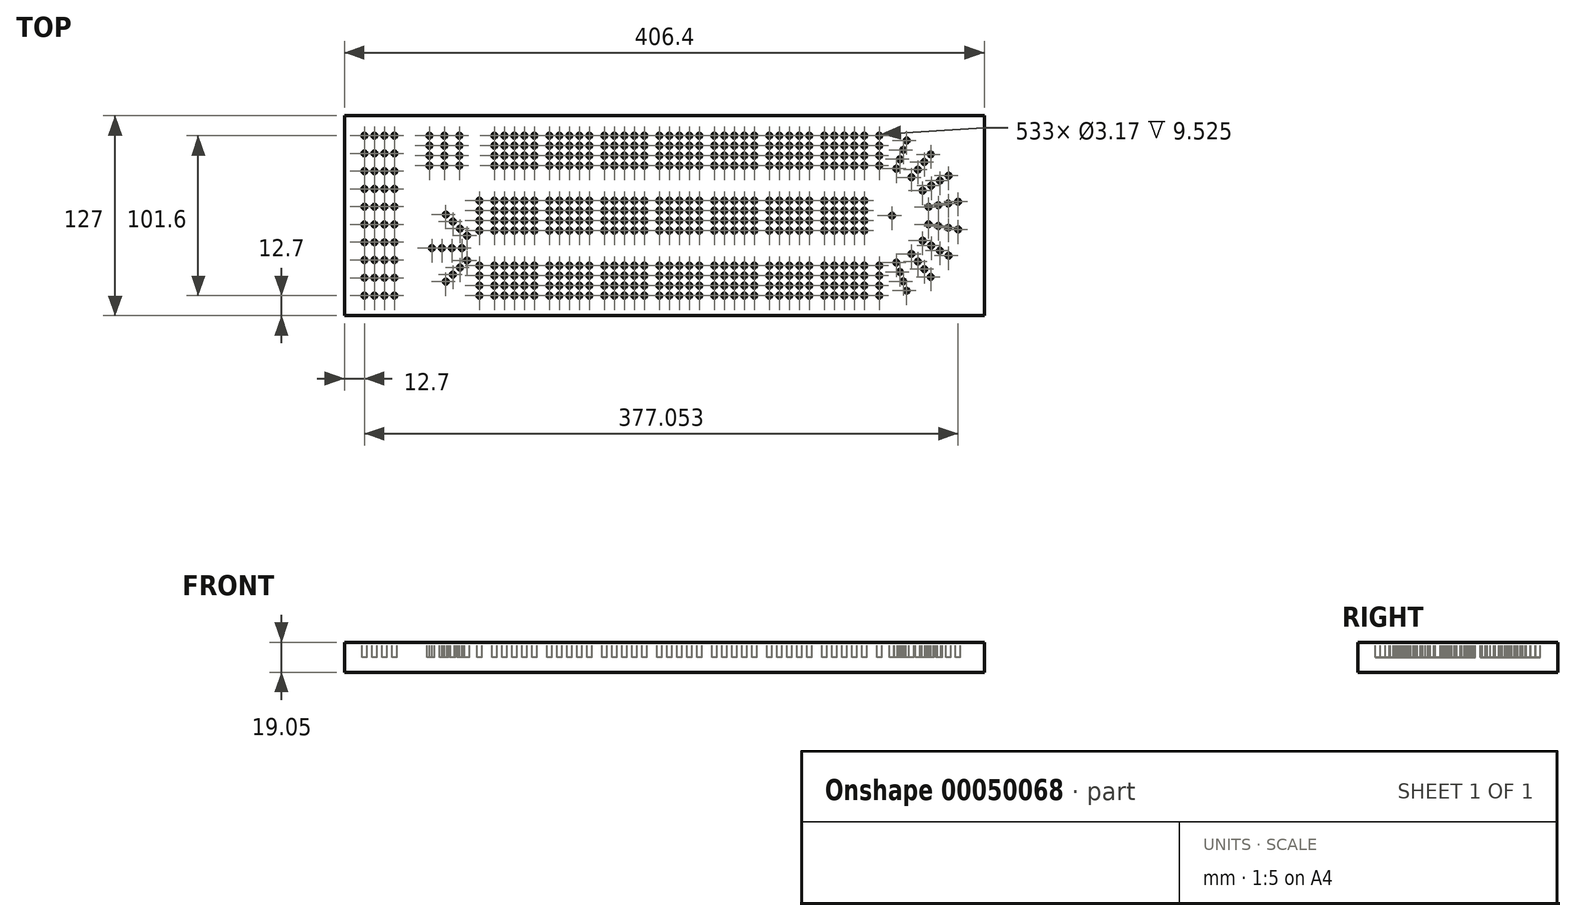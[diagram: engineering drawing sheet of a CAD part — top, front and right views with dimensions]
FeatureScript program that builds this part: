
annotation { "Feature Type Name" : "Feature", "Feature Type Description" : "" }
export const myFeature = defineFeature(function(context is Context, id is Id, definition is map)
    precondition{}
    {
        {
            var Q0;
            Q0=qCreatedBy(makeId("Top.planeOp"),FACE);
            var sketch = newSketch(context, id + "F0", { "sketchPlane" : qUnion([Q0])});
            skLineSegment(sketch, "E0.bottom", {"start": v(0, 0) * mm, "end": v(381, 0) * mm});
            skLineSegment(sketch, "E0.top", {"start": v(0, 127) * mm, "end": v(381, 127) * mm});
            skLineSegment(sketch, "E0.right", {"start": v(381, 0) * mm, "end": v(381, 127) * mm});
            skLineSegment(sketch, "E1", {"start": v(0, 127) * mm, "end": v(-25.4, 127) * mm});
            skLineSegment(sketch, "E2", {"start": v(-25.4, 127) * mm, "end": v(-25.4, 0) * mm});
            skLineSegment(sketch, "E3", {"start": v(-25.4, 0) * mm, "end": v(0, 0) * mm});
            skSolve(sketch);
        }
        {
            var Q0;
            Q0 = qSketchRegion(id + "F0", true);
            extrude(context, id + "F1", {"entities" : qUnion([Q0]), "depth" : 19.05 * mm});
        }
        {
            var Q0;
            Q0=makeQuery(id+"F1.opExtrude","CAP_FACE",FACE,{"disambiguationData":[OSD([sQuery(id+"F0.wireOp",EDGE,"E0.bottom"),sQuery(id+"F0.wireOp",EDGE,"E0.top"),sQuery(id+"F0.wireOp",EDGE,"E0.left"),sQuery(id+"F0.wireOp",EDGE,"E0.right")])],"isStart":false});
            var sketch = newSketch(context, id + "F2", { "sketchPlane" : qUnion([Q0])});
            skCircle(sketch, "E4", {"center": v(69.85, 114.3) * mm, "radius": 1.59 * mm});
            skCircle(sketch, "E5.0.1.0", {"center": v(69.85, 107.95) * mm, "radius": 1.59 * mm});
            skCircle(sketch, "E5.0.2.0", {"center": v(69.85, 101.6) * mm, "radius": 1.59 * mm});
            skCircle(sketch, "E5.0.3.0", {"center": v(69.85, 95.25) * mm, "radius": 1.59 * mm});
            skCircle(sketch, "E5.1.0.0", {"center": v(76.2, 114.3) * mm, "radius": 1.59 * mm});
            skCircle(sketch, "E5.1.1.0", {"center": v(76.2, 107.95) * mm, "radius": 1.59 * mm});
            skCircle(sketch, "E5.1.2.0", {"center": v(76.2, 101.6) * mm, "radius": 1.59 * mm});
            skCircle(sketch, "E5.1.3.0", {"center": v(76.2, 95.25) * mm, "radius": 1.59 * mm});
            skCircle(sketch, "E5.2.0.0", {"center": v(82.55, 114.3) * mm, "radius": 1.59 * mm});
            skCircle(sketch, "E5.2.1.0", {"center": v(82.55, 107.95) * mm, "radius": 1.59 * mm});
            skCircle(sketch, "E5.2.2.0", {"center": v(82.55, 101.6) * mm, "radius": 1.59 * mm});
            skCircle(sketch, "E5.2.3.0", {"center": v(82.55, 95.25) * mm, "radius": 1.59 * mm});
            skCircle(sketch, "E5.3.0.0", {"center": v(88.9, 114.3) * mm, "radius": 1.59 * mm});
            skCircle(sketch, "E5.3.1.0", {"center": v(88.9, 107.95) * mm, "radius": 1.59 * mm});
            skCircle(sketch, "E5.3.2.0", {"center": v(88.9, 101.6) * mm, "radius": 1.59 * mm});
            skCircle(sketch, "E5.3.3.0", {"center": v(88.9, 95.25) * mm, "radius": 1.59 * mm});
            skCircle(sketch, "E5.4.0.0", {"center": v(95.25, 114.3) * mm, "radius": 1.59 * mm});
            skCircle(sketch, "E5.4.1.0", {"center": v(95.25, 107.95) * mm, "radius": 1.59 * mm});
            skCircle(sketch, "E5.4.2.0", {"center": v(95.25, 101.6) * mm, "radius": 1.59 * mm});
            skCircle(sketch, "E5.4.3.0", {"center": v(95.25, 95.25) * mm, "radius": 1.59 * mm});
            skLineSegment(sketch, "E5.direction1", {"start": v(69.85, 114.3) * mm, "end": v(76.2, 114.3) * mm, "construction": true});
            skLineSegment(sketch, "E5.direction2", {"start": v(69.85, 114.3) * mm, "end": v(69.85, 107.95) * mm, "construction": true});
            skCircle(sketch, "E6.1.0.0", {"center": v(123.82, 95.25) * mm, "radius": 1.59 * mm});
            skCircle(sketch, "E6.1.0.1", {"center": v(117.47, 95.25) * mm, "radius": 1.59 * mm});
            skCircle(sketch, "E6.1.0.2", {"center": v(117.47, 114.3) * mm, "radius": 1.59 * mm});
            skCircle(sketch, "E6.1.0.3", {"center": v(130.17, 95.25) * mm, "radius": 1.59 * mm});
            skCircle(sketch, "E6.1.0.4", {"center": v(117.47, 107.95) * mm, "radius": 1.59 * mm});
            skCircle(sketch, "E6.1.0.5", {"center": v(130.17, 114.3) * mm, "radius": 1.59 * mm});
            skCircle(sketch, "E6.1.0.6", {"center": v(123.82, 114.3) * mm, "radius": 1.59 * mm});
            skCircle(sketch, "E6.1.0.7", {"center": v(123.82, 107.95) * mm, "radius": 1.59 * mm});
            skCircle(sketch, "E6.1.0.8", {"center": v(111.12, 95.25) * mm, "radius": 1.59 * mm});
            skCircle(sketch, "E6.1.0.9", {"center": v(123.82, 101.6) * mm, "radius": 1.59 * mm});
            skCircle(sketch, "E6.1.0.10", {"center": v(130.17, 107.95) * mm, "radius": 1.59 * mm});
            skCircle(sketch, "E6.1.0.11", {"center": v(111.12, 107.95) * mm, "radius": 1.59 * mm});
            skCircle(sketch, "E6.1.0.12", {"center": v(117.47, 101.6) * mm, "radius": 1.59 * mm});
            skCircle(sketch, "E6.1.0.13", {"center": v(104.78, 101.6) * mm, "radius": 1.59 * mm});
            skCircle(sketch, "E6.1.0.14", {"center": v(130.17, 101.6) * mm, "radius": 1.59 * mm});
            skCircle(sketch, "E6.1.0.15", {"center": v(111.12, 101.6) * mm, "radius": 1.59 * mm});
            skLineSegment(sketch, "E6.1.0.16", {"start": v(104.78, 114.3) * mm, "end": v(111.12, 114.3) * mm, "construction": true});
            skCircle(sketch, "E6.1.0.17", {"center": v(111.12, 114.3) * mm, "radius": 1.59 * mm});
            skLineSegment(sketch, "E6.1.0.18", {"start": v(104.78, 114.3) * mm, "end": v(104.78, 107.95) * mm, "construction": true});
            skCircle(sketch, "E6.1.0.19", {"center": v(104.78, 107.95) * mm, "radius": 1.59 * mm});
            skCircle(sketch, "E6.1.0.20", {"center": v(104.78, 114.3) * mm, "radius": 1.59 * mm});
            skCircle(sketch, "E6.1.0.21", {"center": v(104.78, 95.25) * mm, "radius": 1.59 * mm});
            skCircle(sketch, "E6.2.0.0", {"center": v(158.75, 95.25) * mm, "radius": 1.59 * mm});
            skCircle(sketch, "E6.2.0.1", {"center": v(152.4, 95.25) * mm, "radius": 1.59 * mm});
            skCircle(sketch, "E6.2.0.2", {"center": v(152.4, 114.3) * mm, "radius": 1.59 * mm});
            skCircle(sketch, "E6.2.0.3", {"center": v(165.1, 95.25) * mm, "radius": 1.59 * mm});
            skCircle(sketch, "E6.2.0.4", {"center": v(152.4, 107.95) * mm, "radius": 1.59 * mm});
            skCircle(sketch, "E6.2.0.5", {"center": v(165.1, 114.3) * mm, "radius": 1.59 * mm});
            skCircle(sketch, "E6.2.0.6", {"center": v(158.75, 114.3) * mm, "radius": 1.59 * mm});
            skCircle(sketch, "E6.2.0.7", {"center": v(158.75, 107.95) * mm, "radius": 1.59 * mm});
            skCircle(sketch, "E6.2.0.8", {"center": v(146.05, 95.25) * mm, "radius": 1.59 * mm});
            skCircle(sketch, "E6.2.0.9", {"center": v(158.75, 101.6) * mm, "radius": 1.59 * mm});
            skCircle(sketch, "E6.2.0.10", {"center": v(165.1, 107.95) * mm, "radius": 1.59 * mm});
            skCircle(sketch, "E6.2.0.11", {"center": v(146.05, 107.95) * mm, "radius": 1.59 * mm});
            skCircle(sketch, "E6.2.0.12", {"center": v(152.4, 101.6) * mm, "radius": 1.59 * mm});
            skCircle(sketch, "E6.2.0.13", {"center": v(139.7, 101.6) * mm, "radius": 1.59 * mm});
            skCircle(sketch, "E6.2.0.14", {"center": v(165.1, 101.6) * mm, "radius": 1.59 * mm});
            skCircle(sketch, "E6.2.0.15", {"center": v(146.05, 101.6) * mm, "radius": 1.59 * mm});
            skLineSegment(sketch, "E6.2.0.16", {"start": v(139.7, 114.3) * mm, "end": v(146.05, 114.3) * mm, "construction": true});
            skCircle(sketch, "E6.2.0.17", {"center": v(146.05, 114.3) * mm, "radius": 1.59 * mm});
            skLineSegment(sketch, "E6.2.0.18", {"start": v(139.7, 114.3) * mm, "end": v(139.7, 107.95) * mm, "construction": true});
            skCircle(sketch, "E6.2.0.19", {"center": v(139.7, 107.95) * mm, "radius": 1.59 * mm});
            skCircle(sketch, "E6.2.0.20", {"center": v(139.7, 114.3) * mm, "radius": 1.59 * mm});
            skCircle(sketch, "E6.2.0.21", {"center": v(139.7, 95.25) * mm, "radius": 1.59 * mm});
            skCircle(sketch, "E6.3.0.0", {"center": v(193.68, 95.25) * mm, "radius": 1.59 * mm});
            skCircle(sketch, "E6.3.0.1", {"center": v(187.33, 95.25) * mm, "radius": 1.59 * mm});
            skCircle(sketch, "E6.3.0.2", {"center": v(187.33, 114.3) * mm, "radius": 1.59 * mm});
            skCircle(sketch, "E6.3.0.3", {"center": v(200.03, 95.25) * mm, "radius": 1.59 * mm});
            skCircle(sketch, "E6.3.0.4", {"center": v(187.33, 107.95) * mm, "radius": 1.59 * mm});
            skCircle(sketch, "E6.3.0.5", {"center": v(200.03, 114.3) * mm, "radius": 1.59 * mm});
            skCircle(sketch, "E6.3.0.6", {"center": v(193.68, 114.3) * mm, "radius": 1.59 * mm});
            skCircle(sketch, "E6.3.0.7", {"center": v(193.68, 107.95) * mm, "radius": 1.59 * mm});
            skCircle(sketch, "E6.3.0.8", {"center": v(180.98, 95.25) * mm, "radius": 1.59 * mm});
            skCircle(sketch, "E6.3.0.9", {"center": v(193.68, 101.6) * mm, "radius": 1.59 * mm});
            skCircle(sketch, "E6.3.0.10", {"center": v(200.03, 107.95) * mm, "radius": 1.59 * mm});
            skCircle(sketch, "E6.3.0.11", {"center": v(180.98, 107.95) * mm, "radius": 1.59 * mm});
            skCircle(sketch, "E6.3.0.12", {"center": v(187.33, 101.6) * mm, "radius": 1.59 * mm});
            skCircle(sketch, "E6.3.0.13", {"center": v(174.63, 101.6) * mm, "radius": 1.59 * mm});
            skCircle(sketch, "E6.3.0.14", {"center": v(200.03, 101.6) * mm, "radius": 1.59 * mm});
            skCircle(sketch, "E6.3.0.15", {"center": v(180.98, 101.6) * mm, "radius": 1.59 * mm});
            skLineSegment(sketch, "E6.3.0.16", {"start": v(174.63, 114.3) * mm, "end": v(180.97, 114.3) * mm, "construction": true});
            skCircle(sketch, "E6.3.0.17", {"center": v(180.98, 114.3) * mm, "radius": 1.59 * mm});
            skLineSegment(sketch, "E6.3.0.18", {"start": v(174.63, 114.3) * mm, "end": v(174.63, 107.95) * mm, "construction": true});
            skCircle(sketch, "E6.3.0.19", {"center": v(174.63, 107.95) * mm, "radius": 1.59 * mm});
            skCircle(sketch, "E6.3.0.20", {"center": v(174.63, 114.3) * mm, "radius": 1.59 * mm});
            skCircle(sketch, "E6.3.0.21", {"center": v(174.63, 95.25) * mm, "radius": 1.59 * mm});
            skCircle(sketch, "E6.4.0.0", {"center": v(228.6, 95.25) * mm, "radius": 1.59 * mm});
            skCircle(sketch, "E6.4.0.1", {"center": v(222.25, 95.25) * mm, "radius": 1.59 * mm});
            skCircle(sketch, "E6.4.0.2", {"center": v(222.25, 114.3) * mm, "radius": 1.59 * mm});
            skCircle(sketch, "E6.4.0.3", {"center": v(234.95, 95.25) * mm, "radius": 1.59 * mm});
            skCircle(sketch, "E6.4.0.4", {"center": v(222.25, 107.95) * mm, "radius": 1.59 * mm});
            skCircle(sketch, "E6.4.0.5", {"center": v(234.95, 114.3) * mm, "radius": 1.59 * mm});
            skCircle(sketch, "E6.4.0.6", {"center": v(228.6, 114.3) * mm, "radius": 1.59 * mm});
            skCircle(sketch, "E6.4.0.7", {"center": v(228.6, 107.95) * mm, "radius": 1.59 * mm});
            skCircle(sketch, "E6.4.0.8", {"center": v(215.9, 95.25) * mm, "radius": 1.59 * mm});
            skCircle(sketch, "E6.4.0.9", {"center": v(228.6, 101.6) * mm, "radius": 1.59 * mm});
            skCircle(sketch, "E6.4.0.10", {"center": v(234.95, 107.95) * mm, "radius": 1.59 * mm});
            skCircle(sketch, "E6.4.0.11", {"center": v(215.9, 107.95) * mm, "radius": 1.59 * mm});
            skCircle(sketch, "E6.4.0.12", {"center": v(222.25, 101.6) * mm, "radius": 1.59 * mm});
            skCircle(sketch, "E6.4.0.13", {"center": v(209.55, 101.6) * mm, "radius": 1.59 * mm});
            skCircle(sketch, "E6.4.0.14", {"center": v(234.95, 101.6) * mm, "radius": 1.59 * mm});
            skCircle(sketch, "E6.4.0.15", {"center": v(215.9, 101.6) * mm, "radius": 1.59 * mm});
            skLineSegment(sketch, "E6.4.0.16", {"start": v(209.55, 114.3) * mm, "end": v(215.9, 114.3) * mm, "construction": true});
            skCircle(sketch, "E6.4.0.17", {"center": v(215.9, 114.3) * mm, "radius": 1.59 * mm});
            skLineSegment(sketch, "E6.4.0.18", {"start": v(209.55, 114.3) * mm, "end": v(209.55, 107.95) * mm, "construction": true});
            skCircle(sketch, "E6.4.0.19", {"center": v(209.55, 107.95) * mm, "radius": 1.59 * mm});
            skCircle(sketch, "E6.4.0.20", {"center": v(209.55, 114.3) * mm, "radius": 1.59 * mm});
            skCircle(sketch, "E6.4.0.21", {"center": v(209.55, 95.25) * mm, "radius": 1.59 * mm});
            skCircle(sketch, "E6.5.0.0", {"center": v(263.53, 95.25) * mm, "radius": 1.59 * mm});
            skCircle(sketch, "E6.5.0.1", {"center": v(257.18, 95.25) * mm, "radius": 1.59 * mm});
            skCircle(sketch, "E6.5.0.2", {"center": v(257.18, 114.3) * mm, "radius": 1.59 * mm});
            skCircle(sketch, "E6.5.0.3", {"center": v(269.88, 95.25) * mm, "radius": 1.59 * mm});
            skCircle(sketch, "E6.5.0.4", {"center": v(257.18, 107.95) * mm, "radius": 1.59 * mm});
            skCircle(sketch, "E6.5.0.5", {"center": v(269.88, 114.3) * mm, "radius": 1.59 * mm});
            skCircle(sketch, "E6.5.0.6", {"center": v(263.53, 114.3) * mm, "radius": 1.59 * mm});
            skCircle(sketch, "E6.5.0.7", {"center": v(263.53, 107.95) * mm, "radius": 1.59 * mm});
            skCircle(sketch, "E6.5.0.8", {"center": v(250.83, 95.25) * mm, "radius": 1.59 * mm});
            skCircle(sketch, "E6.5.0.9", {"center": v(263.53, 101.6) * mm, "radius": 1.59 * mm});
            skCircle(sketch, "E6.5.0.10", {"center": v(269.88, 107.95) * mm, "radius": 1.59 * mm});
            skCircle(sketch, "E6.5.0.11", {"center": v(250.83, 107.95) * mm, "radius": 1.59 * mm});
            skCircle(sketch, "E6.5.0.12", {"center": v(257.18, 101.6) * mm, "radius": 1.59 * mm});
            skCircle(sketch, "E6.5.0.13", {"center": v(244.48, 101.6) * mm, "radius": 1.59 * mm});
            skCircle(sketch, "E6.5.0.14", {"center": v(269.88, 101.6) * mm, "radius": 1.59 * mm});
            skCircle(sketch, "E6.5.0.15", {"center": v(250.83, 101.6) * mm, "radius": 1.59 * mm});
            skLineSegment(sketch, "E6.5.0.16", {"start": v(244.48, 114.3) * mm, "end": v(250.83, 114.3) * mm, "construction": true});
            skCircle(sketch, "E6.5.0.17", {"center": v(250.83, 114.3) * mm, "radius": 1.59 * mm});
            skLineSegment(sketch, "E6.5.0.18", {"start": v(244.48, 114.3) * mm, "end": v(244.48, 107.95) * mm, "construction": true});
            skCircle(sketch, "E6.5.0.19", {"center": v(244.48, 107.95) * mm, "radius": 1.59 * mm});
            skCircle(sketch, "E6.5.0.20", {"center": v(244.48, 114.3) * mm, "radius": 1.59 * mm});
            skCircle(sketch, "E6.5.0.21", {"center": v(244.48, 95.25) * mm, "radius": 1.59 * mm});
            skCircle(sketch, "E6.6.0.0", {"center": v(298.45, 95.25) * mm, "radius": 1.59 * mm});
            skCircle(sketch, "E6.6.0.1", {"center": v(292.1, 95.25) * mm, "radius": 1.59 * mm});
            skCircle(sketch, "E6.6.0.2", {"center": v(292.1, 114.3) * mm, "radius": 1.59 * mm});
            skCircle(sketch, "E6.6.0.3", {"center": v(304.8, 95.25) * mm, "radius": 1.59 * mm});
            skCircle(sketch, "E6.6.0.4", {"center": v(292.1, 107.95) * mm, "radius": 1.59 * mm});
            skCircle(sketch, "E6.6.0.5", {"center": v(304.8, 114.3) * mm, "radius": 1.59 * mm});
            skCircle(sketch, "E6.6.0.6", {"center": v(298.45, 114.3) * mm, "radius": 1.59 * mm});
            skCircle(sketch, "E6.6.0.7", {"center": v(298.45, 107.95) * mm, "radius": 1.59 * mm});
            skCircle(sketch, "E6.6.0.8", {"center": v(285.75, 95.25) * mm, "radius": 1.59 * mm});
            skCircle(sketch, "E6.6.0.9", {"center": v(298.45, 101.6) * mm, "radius": 1.59 * mm});
            skCircle(sketch, "E6.6.0.10", {"center": v(304.8, 107.95) * mm, "radius": 1.59 * mm});
            skCircle(sketch, "E6.6.0.11", {"center": v(285.75, 107.95) * mm, "radius": 1.59 * mm});
            skCircle(sketch, "E6.6.0.12", {"center": v(292.1, 101.6) * mm, "radius": 1.59 * mm});
            skCircle(sketch, "E6.6.0.13", {"center": v(279.4, 101.6) * mm, "radius": 1.59 * mm});
            skCircle(sketch, "E6.6.0.14", {"center": v(304.8, 101.6) * mm, "radius": 1.59 * mm});
            skCircle(sketch, "E6.6.0.15", {"center": v(285.75, 101.6) * mm, "radius": 1.59 * mm});
            skLineSegment(sketch, "E6.6.0.16", {"start": v(279.4, 114.3) * mm, "end": v(285.75, 114.3) * mm, "construction": true});
            skCircle(sketch, "E6.6.0.17", {"center": v(285.75, 114.3) * mm, "radius": 1.59 * mm});
            skLineSegment(sketch, "E6.6.0.18", {"start": v(279.4, 114.3) * mm, "end": v(279.4, 107.95) * mm, "construction": true});
            skCircle(sketch, "E6.6.0.19", {"center": v(279.4, 107.95) * mm, "radius": 1.59 * mm});
            skCircle(sketch, "E6.6.0.20", {"center": v(279.4, 114.3) * mm, "radius": 1.59 * mm});
            skCircle(sketch, "E6.6.0.21", {"center": v(279.4, 95.25) * mm, "radius": 1.59 * mm});
            skLineSegment(sketch, "E6.direction1", {"start": v(88.9, 95.25) * mm, "end": v(123.82, 95.25) * mm, "construction": true});
            skLineSegment(sketch, "E7.MirrorCS", {"start": v(69.85, 12.7) * mm, "end": v(69.85, 19.05) * mm, "construction": true});
            skCircle(sketch, "E8.MirrorC", {"center": v(174.63, 12.7) * mm, "radius": 1.59 * mm});
            skLineSegment(sketch, "E9.MirrorCS", {"start": v(279.4, 12.7) * mm, "end": v(279.4, 19.05) * mm, "construction": true});
            skLineSegment(sketch, "E10.MirrorCS", {"start": v(104.78, 12.7) * mm, "end": v(104.78, 19.05) * mm, "construction": true});
            skLineSegment(sketch, "E11.MirrorCS", {"start": v(209.55, 12.7) * mm, "end": v(215.9, 12.7) * mm, "construction": true});
            skCircle(sketch, "E12.MirrorC", {"center": v(279.4, 12.7) * mm, "radius": 1.59 * mm});
            skCircle(sketch, "E13.MirrorC", {"center": v(104.78, 12.7) * mm, "radius": 1.59 * mm});
            skLineSegment(sketch, "E14.MirrorCS", {"start": v(209.55, 12.7) * mm, "end": v(209.55, 19.05) * mm, "construction": true});
            skLineSegment(sketch, "E15.MirrorCS", {"start": v(139.7, 12.7) * mm, "end": v(146.05, 12.7) * mm, "construction": true});
            skCircle(sketch, "E16.MirrorC", {"center": v(209.55, 12.7) * mm, "radius": 1.59 * mm});
            skLineSegment(sketch, "E17.MirrorCS", {"start": v(139.7, 12.7) * mm, "end": v(139.7, 19.05) * mm, "construction": true});
            skLineSegment(sketch, "E18.MirrorCS", {"start": v(244.48, 12.7) * mm, "end": v(250.83, 12.7) * mm, "construction": true});
            skCircle(sketch, "E19.MirrorC", {"center": v(139.7, 12.7) * mm, "radius": 1.59 * mm});
            skCircle(sketch, "E20.MirrorC", {"center": v(69.85, 12.7) * mm, "radius": 1.59 * mm});
            skLineSegment(sketch, "E21.MirrorCS", {"start": v(244.48, 12.7) * mm, "end": v(244.48, 19.05) * mm, "construction": true});
            skCircle(sketch, "E22.MirrorC", {"center": v(244.48, 12.7) * mm, "radius": 1.59 * mm});
            skLineSegment(sketch, "E23.MirrorCS", {"start": v(174.63, 12.7) * mm, "end": v(180.97, 12.7) * mm, "construction": true});
            skLineSegment(sketch, "E24.MirrorCS", {"start": v(174.63, 12.7) * mm, "end": v(174.63, 19.05) * mm, "construction": true});
            skLineSegment(sketch, "E25.MirrorCS", {"start": v(69.85, 12.7) * mm, "end": v(76.2, 12.7) * mm, "construction": true});
            skCircle(sketch, "E26.MirrorC", {"center": v(174.63, 19.05) * mm, "radius": 1.59 * mm});
            skCircle(sketch, "E27.MirrorC", {"center": v(285.75, 12.7) * mm, "radius": 1.59 * mm});
            skCircle(sketch, "E28.MirrorC", {"center": v(111.12, 12.7) * mm, "radius": 1.59 * mm});
            skCircle(sketch, "E29.MirrorC", {"center": v(279.4, 19.05) * mm, "radius": 1.59 * mm});
            skLineSegment(sketch, "E30.MirrorCS", {"start": v(104.78, 12.7) * mm, "end": v(111.12, 12.7) * mm, "construction": true});
            skCircle(sketch, "E31.MirrorC", {"center": v(123.82, 31.75) * mm, "radius": 1.59 * mm});
            skCircle(sketch, "E32.MirrorC", {"center": v(104.78, 19.05) * mm, "radius": 1.59 * mm});
            skCircle(sketch, "E33.MirrorC", {"center": v(215.9, 12.7) * mm, "radius": 1.59 * mm});
            skCircle(sketch, "E34.MirrorC", {"center": v(209.55, 19.05) * mm, "radius": 1.59 * mm});
            skCircle(sketch, "E35.MirrorC", {"center": v(146.05, 12.7) * mm, "radius": 1.59 * mm});
            skCircle(sketch, "E36.MirrorC", {"center": v(139.7, 19.05) * mm, "radius": 1.59 * mm});
            skCircle(sketch, "E37.MirrorC", {"center": v(88.9, 31.75) * mm, "radius": 1.59 * mm});
            skCircle(sketch, "E38.MirrorC", {"center": v(250.83, 12.7) * mm, "radius": 1.59 * mm});
            skCircle(sketch, "E39.MirrorC", {"center": v(69.85, 19.05) * mm, "radius": 1.59 * mm});
            skCircle(sketch, "E40.MirrorC", {"center": v(180.98, 12.7) * mm, "radius": 1.59 * mm});
            skLineSegment(sketch, "E41.MirrorCS", {"start": v(279.4, 12.7) * mm, "end": v(285.75, 12.7) * mm, "construction": true});
            skCircle(sketch, "E42.MirrorC", {"center": v(76.2, 12.7) * mm, "radius": 1.59 * mm});
            skCircle(sketch, "E43.MirrorC", {"center": v(244.48, 19.05) * mm, "radius": 1.59 * mm});
            skCircle(sketch, "E44.MirrorC", {"center": v(111.12, 25.4) * mm, "radius": 1.59 * mm});
            skCircle(sketch, "E45.MirrorC", {"center": v(76.2, 19.05) * mm, "radius": 1.59 * mm});
            skCircle(sketch, "E46.MirrorC", {"center": v(209.55, 25.4) * mm, "radius": 1.59 * mm});
            skCircle(sketch, "E47.MirrorC", {"center": v(200.03, 31.75) * mm, "radius": 1.59 * mm});
            skCircle(sketch, "E48.MirrorC", {"center": v(158.75, 25.4) * mm, "radius": 1.59 * mm});
            skCircle(sketch, "E49.MirrorC", {"center": v(292.1, 31.75) * mm, "radius": 1.59 * mm});
            skCircle(sketch, "E50.MirrorC", {"center": v(263.53, 19.05) * mm, "radius": 1.59 * mm});
            skCircle(sketch, "E51.MirrorC", {"center": v(146.05, 19.05) * mm, "radius": 1.59 * mm});
            skCircle(sketch, "E52.MirrorC", {"center": v(117.47, 31.75) * mm, "radius": 1.59 * mm});
            skCircle(sketch, "E53.MirrorC", {"center": v(76.2, 31.75) * mm, "radius": 1.59 * mm});
            skCircle(sketch, "E54.MirrorC", {"center": v(263.53, 25.4) * mm, "radius": 1.59 * mm});
            skCircle(sketch, "E55.MirrorC", {"center": v(215.9, 25.4) * mm, "radius": 1.59 * mm});
            skCircle(sketch, "E56.MirrorC", {"center": v(174.63, 31.75) * mm, "radius": 1.59 * mm});
            skCircle(sketch, "E57.MirrorC", {"center": v(200.03, 12.7) * mm, "radius": 1.59 * mm});
            skCircle(sketch, "E58.MirrorC", {"center": v(304.8, 31.75) * mm, "radius": 1.59 * mm});
            skCircle(sketch, "E59.MirrorC", {"center": v(76.2, 25.4) * mm, "radius": 1.59 * mm});
            skCircle(sketch, "E60.MirrorC", {"center": v(234.95, 25.4) * mm, "radius": 1.59 * mm});
            skCircle(sketch, "E61.MirrorC", {"center": v(165.1, 19.05) * mm, "radius": 1.59 * mm});
            skCircle(sketch, "E62.MirrorC", {"center": v(187.33, 19.05) * mm, "radius": 1.59 * mm});
            skCircle(sketch, "E63.MirrorC", {"center": v(292.1, 12.7) * mm, "radius": 1.59 * mm});
            skCircle(sketch, "E64.MirrorC", {"center": v(250.83, 31.75) * mm, "radius": 1.59 * mm});
            skCircle(sketch, "E65.MirrorC", {"center": v(152.4, 25.4) * mm, "radius": 1.59 * mm});
            skCircle(sketch, "E66.MirrorC", {"center": v(117.47, 12.7) * mm, "radius": 1.59 * mm});
            skCircle(sketch, "E67.MirrorC", {"center": v(82.55, 12.7) * mm, "radius": 1.59 * mm});
            skCircle(sketch, "E68.MirrorC", {"center": v(269.88, 19.05) * mm, "radius": 1.59 * mm});
            skCircle(sketch, "E69.MirrorC", {"center": v(228.6, 31.75) * mm, "radius": 1.59 * mm});
            skCircle(sketch, "E70.MirrorC", {"center": v(193.68, 12.7) * mm, "radius": 1.59 * mm});
            skCircle(sketch, "E71.MirrorC", {"center": v(292.1, 19.05) * mm, "radius": 1.59 * mm});
            skCircle(sketch, "E72.MirrorC", {"center": v(139.7, 25.4) * mm, "radius": 1.59 * mm});
            skCircle(sketch, "E73.MirrorC", {"center": v(130.17, 31.75) * mm, "radius": 1.59 * mm});
            skCircle(sketch, "E74.MirrorC", {"center": v(82.55, 19.05) * mm, "radius": 1.59 * mm});
            skCircle(sketch, "E75.MirrorC", {"center": v(250.83, 19.05) * mm, "radius": 1.59 * mm});
            skCircle(sketch, "E76.MirrorC", {"center": v(222.25, 31.75) * mm, "radius": 1.59 * mm});
            skCircle(sketch, "E77.MirrorC", {"center": v(193.68, 19.05) * mm, "radius": 1.59 * mm});
            skCircle(sketch, "E78.MirrorC", {"center": v(279.4, 31.75) * mm, "radius": 1.59 * mm});
            skCircle(sketch, "E79.MirrorC", {"center": v(304.8, 12.7) * mm, "radius": 1.59 * mm});
            skCircle(sketch, "E80.MirrorC", {"center": v(165.1, 25.4) * mm, "radius": 1.59 * mm});
            skCircle(sketch, "E81.MirrorC", {"center": v(117.47, 19.05) * mm, "radius": 1.59 * mm});
            skCircle(sketch, "E82.MirrorC", {"center": v(82.55, 25.4) * mm, "radius": 1.59 * mm});
            skCircle(sketch, "E83.MirrorC", {"center": v(257.18, 25.4) * mm, "radius": 1.59 * mm});
            skCircle(sketch, "E84.MirrorC", {"center": v(222.25, 12.7) * mm, "radius": 1.59 * mm});
            skCircle(sketch, "E85.MirrorC", {"center": v(180.98, 31.75) * mm, "radius": 1.59 * mm});
            skCircle(sketch, "E86.MirrorC", {"center": v(298.45, 12.7) * mm, "radius": 1.59 * mm});
            skCircle(sketch, "E87.MirrorC", {"center": v(244.48, 25.4) * mm, "radius": 1.59 * mm});
            skCircle(sketch, "E88.MirrorC", {"center": v(234.95, 31.75) * mm, "radius": 1.59 * mm});
            skCircle(sketch, "E89.MirrorC", {"center": v(193.68, 25.4) * mm, "radius": 1.59 * mm});
            skCircle(sketch, "E90.MirrorC", {"center": v(298.45, 19.05) * mm, "radius": 1.59 * mm});
            skCircle(sketch, "E91.MirrorC", {"center": v(146.05, 25.4) * mm, "radius": 1.59 * mm});
            skCircle(sketch, "E92.MirrorC", {"center": v(104.78, 31.75) * mm, "radius": 1.59 * mm});
            skCircle(sketch, "E93.MirrorC", {"center": v(130.17, 12.7) * mm, "radius": 1.59 * mm});
            skCircle(sketch, "E94.MirrorC", {"center": v(82.55, 31.75) * mm, "radius": 1.59 * mm});
            skCircle(sketch, "E95.MirrorC", {"center": v(285.75, 31.75) * mm, "radius": 1.59 * mm});
            skCircle(sketch, "E96.MirrorC", {"center": v(158.75, 31.75) * mm, "radius": 1.59 * mm});
            skCircle(sketch, "E97.MirrorC", {"center": v(123.82, 12.7) * mm, "radius": 1.59 * mm});
            skCircle(sketch, "E98.MirrorC", {"center": v(88.9, 12.7) * mm, "radius": 1.59 * mm});
            skCircle(sketch, "E99.MirrorC", {"center": v(269.88, 25.4) * mm, "radius": 1.59 * mm});
            skCircle(sketch, "E100.MirrorC", {"center": v(222.25, 19.05) * mm, "radius": 1.59 * mm});
            skCircle(sketch, "E101.MirrorC", {"center": v(200.03, 19.05) * mm, "radius": 1.59 * mm});
            skCircle(sketch, "E102.MirrorC", {"center": v(152.4, 31.75) * mm, "radius": 1.59 * mm});
            skCircle(sketch, "E103.MirrorC", {"center": v(123.82, 19.05) * mm, "radius": 1.59 * mm});
            skCircle(sketch, "E104.MirrorC", {"center": v(88.9, 19.05) * mm, "radius": 1.59 * mm});
            skCircle(sketch, "E105.MirrorC", {"center": v(250.83, 25.4) * mm, "radius": 1.59 * mm});
            skCircle(sketch, "E106.MirrorC", {"center": v(209.55, 31.75) * mm, "radius": 1.59 * mm});
            skCircle(sketch, "E107.MirrorC", {"center": v(234.95, 12.7) * mm, "radius": 1.59 * mm});
            skCircle(sketch, "E108.MirrorC", {"center": v(180.98, 19.05) * mm, "radius": 1.59 * mm});
            skCircle(sketch, "E109.MirrorC", {"center": v(298.45, 25.4) * mm, "radius": 1.59 * mm});
            skCircle(sketch, "E110.MirrorC", {"center": v(152.4, 12.7) * mm, "radius": 1.59 * mm});
            skCircle(sketch, "E111.MirrorC", {"center": v(111.12, 31.75) * mm, "radius": 1.59 * mm});
            skCircle(sketch, "E112.MirrorC", {"center": v(88.9, 25.4) * mm, "radius": 1.59 * mm});
            skCircle(sketch, "E113.MirrorC", {"center": v(263.53, 31.75) * mm, "radius": 1.59 * mm});
            skCircle(sketch, "E114.MirrorC", {"center": v(228.6, 12.7) * mm, "radius": 1.59 * mm});
            skCircle(sketch, "E115.MirrorC", {"center": v(187.33, 25.4) * mm, "radius": 1.59 * mm});
            skCircle(sketch, "E116.MirrorC", {"center": v(304.8, 19.05) * mm, "radius": 1.59 * mm});
            skCircle(sketch, "E117.MirrorC", {"center": v(165.1, 31.75) * mm, "radius": 1.59 * mm});
            skCircle(sketch, "E118.MirrorC", {"center": v(123.82, 25.4) * mm, "radius": 1.59 * mm});
            skCircle(sketch, "E119.MirrorC", {"center": v(257.18, 31.75) * mm, "radius": 1.59 * mm});
            skCircle(sketch, "E120.MirrorC", {"center": v(228.6, 19.05) * mm, "radius": 1.59 * mm});
            skCircle(sketch, "E121.MirrorC", {"center": v(174.63, 25.4) * mm, "radius": 1.59 * mm});
            skCircle(sketch, "E122.MirrorC", {"center": v(285.75, 19.05) * mm, "radius": 1.59 * mm});
            skCircle(sketch, "E123.MirrorC", {"center": v(152.4, 19.05) * mm, "radius": 1.59 * mm});
            skCircle(sketch, "E124.MirrorC", {"center": v(130.17, 19.05) * mm, "radius": 1.59 * mm});
            skCircle(sketch, "E125.MirrorC", {"center": v(95.25, 12.7) * mm, "radius": 1.59 * mm});
            skCircle(sketch, "E126.MirrorC", {"center": v(69.85, 31.75) * mm, "radius": 1.59 * mm});
            skCircle(sketch, "E127.MirrorC", {"center": v(111.12, 19.05) * mm, "radius": 1.59 * mm});
            skCircle(sketch, "E128.MirrorC", {"center": v(95.25, 19.05) * mm, "radius": 1.59 * mm});
            skCircle(sketch, "E129.MirrorC", {"center": v(180.98, 25.4) * mm, "radius": 1.59 * mm});
            skCircle(sketch, "E130.MirrorC", {"center": v(187.33, 31.75) * mm, "radius": 1.59 * mm});
            skCircle(sketch, "E131.MirrorC", {"center": v(228.6, 25.4) * mm, "radius": 1.59 * mm});
            skCircle(sketch, "E132.MirrorC", {"center": v(285.75, 25.4) * mm, "radius": 1.59 * mm});
            skCircle(sketch, "E133.MirrorC", {"center": v(244.48, 31.75) * mm, "radius": 1.59 * mm});
            skCircle(sketch, "E134.MirrorC", {"center": v(263.53, 12.7) * mm, "radius": 1.59 * mm});
            skCircle(sketch, "E135.MirrorC", {"center": v(104.78, 25.4) * mm, "radius": 1.59 * mm});
            skCircle(sketch, "E136.MirrorC", {"center": v(69.85, 25.4) * mm, "radius": 1.59 * mm});
            skCircle(sketch, "E137.MirrorC", {"center": v(95.25, 25.4) * mm, "radius": 1.59 * mm});
            skCircle(sketch, "E138.MirrorC", {"center": v(257.18, 12.7) * mm, "radius": 1.59 * mm});
            skCircle(sketch, "E139.MirrorC", {"center": v(215.9, 31.75) * mm, "radius": 1.59 * mm});
            skCircle(sketch, "E140.MirrorC", {"center": v(200.03, 25.4) * mm, "radius": 1.59 * mm});
            skCircle(sketch, "E141.MirrorC", {"center": v(292.1, 25.4) * mm, "radius": 1.59 * mm});
            skCircle(sketch, "E142.MirrorC", {"center": v(158.75, 12.7) * mm, "radius": 1.59 * mm});
            skCircle(sketch, "E143.MirrorC", {"center": v(193.68, 31.75) * mm, "radius": 1.59 * mm});
            skCircle(sketch, "E144.MirrorC", {"center": v(95.25, 31.75) * mm, "radius": 1.59 * mm});
            skCircle(sketch, "E145.MirrorC", {"center": v(257.18, 19.05) * mm, "radius": 1.59 * mm});
            skCircle(sketch, "E146.MirrorC", {"center": v(304.8, 25.4) * mm, "radius": 1.59 * mm});
            skCircle(sketch, "E147.MirrorC", {"center": v(215.9, 19.05) * mm, "radius": 1.59 * mm});
            skCircle(sketch, "E148.MirrorC", {"center": v(117.47, 25.4) * mm, "radius": 1.59 * mm});
            skCircle(sketch, "E149.MirrorC", {"center": v(298.45, 31.75) * mm, "radius": 1.59 * mm});
            skCircle(sketch, "E150.MirrorC", {"center": v(146.05, 31.75) * mm, "radius": 1.59 * mm});
            skCircle(sketch, "E151.MirrorC", {"center": v(187.33, 12.7) * mm, "radius": 1.59 * mm});
            skCircle(sketch, "E152.MirrorC", {"center": v(222.25, 25.4) * mm, "radius": 1.59 * mm});
            skCircle(sketch, "E153.MirrorC", {"center": v(130.17, 25.4) * mm, "radius": 1.59 * mm});
            skCircle(sketch, "E154.MirrorC", {"center": v(269.88, 12.7) * mm, "radius": 1.59 * mm});
            skCircle(sketch, "E155.MirrorC", {"center": v(269.88, 31.75) * mm, "radius": 1.59 * mm});
            skCircle(sketch, "E156.MirrorC", {"center": v(234.95, 19.05) * mm, "radius": 1.59 * mm});
            skCircle(sketch, "E157.MirrorC", {"center": v(158.75, 19.05) * mm, "radius": 1.59 * mm});
            skCircle(sketch, "E158.MirrorC", {"center": v(279.4, 25.4) * mm, "radius": 1.59 * mm});
            skCircle(sketch, "E159.MirrorC", {"center": v(139.7, 31.75) * mm, "radius": 1.59 * mm});
            skCircle(sketch, "E160.MirrorC", {"center": v(165.1, 12.7) * mm, "radius": 1.59 * mm});
            skLineSegment(sketch, "E161.MirrorCS", {"start": v(88.9, 31.75) * mm, "end": v(123.82, 31.75) * mm, "construction": true});
            skPoint(sketch, "E162.orphan", {"position": v(393.7, 111.97) * mm});
            skPoint(sketch, "E163.orphan", {"position": v(393.7, 61.17) * mm});
            skCircle(sketch, "E164.MirrorC", {"center": v(139.7, 73.02) * mm, "radius": 1.59 * mm});
            skLineSegment(sketch, "E165.MirrorCS", {"start": v(244.48, 73.02) * mm, "end": v(250.83, 73.02) * mm, "construction": true});
            skLineSegment(sketch, "E166.MirrorCS", {"start": v(139.7, 73.02) * mm, "end": v(139.7, 66.67) * mm, "construction": true});
            skCircle(sketch, "E167.MirrorC", {"center": v(209.55, 73.02) * mm, "radius": 1.59 * mm});
            skLineSegment(sketch, "E168.MirrorCS", {"start": v(139.7, 73.02) * mm, "end": v(146.05, 73.02) * mm, "construction": true});
            skLineSegment(sketch, "E169.MirrorCS", {"start": v(104.77, 73.02) * mm, "end": v(111.12, 73.02) * mm, "construction": true});
            skLineSegment(sketch, "E170.MirrorCS", {"start": v(209.55, 73.02) * mm, "end": v(209.55, 66.67) * mm, "construction": true});
            skLineSegment(sketch, "E171.MirrorCS", {"start": v(69.85, 73.02) * mm, "end": v(69.85, 66.67) * mm, "construction": true});
            skLineSegment(sketch, "E172.MirrorCS", {"start": v(174.63, 73.02) * mm, "end": v(180.98, 73.02) * mm, "construction": true});
            skCircle(sketch, "E173.MirrorC", {"center": v(244.48, 73.02) * mm, "radius": 1.59 * mm});
            skCircle(sketch, "E174.MirrorC", {"center": v(104.77, 73.02) * mm, "radius": 1.59 * mm});
            skLineSegment(sketch, "E175.MirrorCS", {"start": v(244.48, 73.02) * mm, "end": v(244.48, 66.67) * mm, "construction": true});
            skCircle(sketch, "E176.MirrorC", {"center": v(279.4, 73.02) * mm, "radius": 1.59 * mm});
            skLineSegment(sketch, "E177.MirrorCS", {"start": v(209.55, 73.02) * mm, "end": v(215.9, 73.02) * mm, "construction": true});
            skCircle(sketch, "E178.MirrorC", {"center": v(69.85, 73.02) * mm, "radius": 1.59 * mm});
            skLineSegment(sketch, "E179.MirrorCS", {"start": v(104.78, 73.02) * mm, "end": v(104.78, 66.67) * mm, "construction": true});
            skLineSegment(sketch, "E180.MirrorCS", {"start": v(279.4, 73.02) * mm, "end": v(285.75, 73.02) * mm, "construction": true});
            skLineSegment(sketch, "E181.MirrorCS", {"start": v(69.85, 73.02) * mm, "end": v(76.2, 73.02) * mm, "construction": true});
            skLineSegment(sketch, "E182.MirrorCS", {"start": v(279.4, 73.02) * mm, "end": v(279.4, 66.67) * mm, "construction": true});
            skCircle(sketch, "E183.MirrorC", {"center": v(174.63, 73.02) * mm, "radius": 1.59 * mm});
            skCircle(sketch, "E184.MirrorC", {"center": v(146.05, 73.02) * mm, "radius": 1.59 * mm});
            skCircle(sketch, "E185.MirrorC", {"center": v(209.55, 66.67) * mm, "radius": 1.59 * mm});
            skCircle(sketch, "E186.MirrorC", {"center": v(215.9, 73.02) * mm, "radius": 1.59 * mm});
            skCircle(sketch, "E187.MirrorC", {"center": v(104.78, 66.67) * mm, "radius": 1.59 * mm});
            skCircle(sketch, "E188.MirrorC", {"center": v(123.82, 53.97) * mm, "radius": 1.59 * mm});
            skCircle(sketch, "E189.MirrorC", {"center": v(69.85, 66.67) * mm, "radius": 1.59 * mm});
            skCircle(sketch, "E190.MirrorC", {"center": v(250.83, 73.02) * mm, "radius": 1.59 * mm});
            skCircle(sketch, "E191.MirrorC", {"center": v(279.4, 66.67) * mm, "radius": 1.59 * mm});
            skCircle(sketch, "E192.MirrorC", {"center": v(88.9, 53.97) * mm, "radius": 1.59 * mm});
            skCircle(sketch, "E193.MirrorC", {"center": v(111.12, 73.02) * mm, "radius": 1.59 * mm});
            skCircle(sketch, "E194.MirrorC", {"center": v(285.75, 73.02) * mm, "radius": 1.59 * mm});
            skCircle(sketch, "E195.MirrorC", {"center": v(244.48, 66.67) * mm, "radius": 1.59 * mm});
            skCircle(sketch, "E196.MirrorC", {"center": v(139.7, 66.67) * mm, "radius": 1.59 * mm});
            skCircle(sketch, "E197.MirrorC", {"center": v(76.2, 73.02) * mm, "radius": 1.59 * mm});
            skCircle(sketch, "E198.MirrorC", {"center": v(174.63, 66.67) * mm, "radius": 1.59 * mm});
            skCircle(sketch, "E199.MirrorC", {"center": v(180.98, 73.02) * mm, "radius": 1.59 * mm});
            skLineSegment(sketch, "E200.MirrorCS", {"start": v(174.63, 73.02) * mm, "end": v(174.63, 66.67) * mm, "construction": true});
            skCircle(sketch, "E201.MirrorC", {"center": v(269.88, 60.32) * mm, "radius": 1.59 * mm});
            skCircle(sketch, "E202.MirrorC", {"center": v(187.33, 60.32) * mm, "radius": 1.59 * mm});
            skCircle(sketch, "E203.MirrorC", {"center": v(215.9, 66.67) * mm, "radius": 1.59 * mm});
            skCircle(sketch, "E204.MirrorC", {"center": v(228.6, 60.32) * mm, "radius": 1.59 * mm});
            skCircle(sketch, "E205.MirrorC", {"center": v(146.05, 66.67) * mm, "radius": 1.59 * mm});
            skCircle(sketch, "E206.MirrorC", {"center": v(82.55, 73.02) * mm, "radius": 1.59 * mm});
            skCircle(sketch, "E207.MirrorC", {"center": v(257.18, 60.32) * mm, "radius": 1.59 * mm});
            skCircle(sketch, "E208.MirrorC", {"center": v(88.9, 73.02) * mm, "radius": 1.59 * mm});
            skCircle(sketch, "E209.MirrorC", {"center": v(228.6, 73.02) * mm, "radius": 1.59 * mm});
            skCircle(sketch, "E210.MirrorC", {"center": v(187.33, 53.97) * mm, "radius": 1.59 * mm});
            skCircle(sketch, "E211.MirrorC", {"center": v(304.8, 60.33) * mm, "radius": 1.59 * mm});
            skCircle(sketch, "E212.MirrorC", {"center": v(263.53, 66.67) * mm, "radius": 1.59 * mm});
            skCircle(sketch, "E213.MirrorC", {"center": v(117.47, 73.02) * mm, "radius": 1.59 * mm});
            skCircle(sketch, "E214.MirrorC", {"center": v(82.55, 60.32) * mm, "radius": 1.59 * mm});
            skCircle(sketch, "E215.MirrorC", {"center": v(123.82, 73.02) * mm, "radius": 1.59 * mm});
            skCircle(sketch, "E216.MirrorC", {"center": v(263.53, 53.97) * mm, "radius": 1.59 * mm});
            skCircle(sketch, "E217.MirrorC", {"center": v(180.98, 60.32) * mm, "radius": 1.59 * mm});
            skCircle(sketch, "E218.MirrorC", {"center": v(257.18, 66.67) * mm, "radius": 1.59 * mm});
            skCircle(sketch, "E219.MirrorC", {"center": v(292.1, 53.98) * mm, "radius": 1.59 * mm});
            skCircle(sketch, "E220.MirrorC", {"center": v(152.4, 60.32) * mm, "radius": 1.59 * mm});
            skCircle(sketch, "E221.MirrorC", {"center": v(117.47, 66.67) * mm, "radius": 1.59 * mm});
            skCircle(sketch, "E222.MirrorC", {"center": v(165.1, 73.02) * mm, "radius": 1.59 * mm});
            skCircle(sketch, "E223.MirrorC", {"center": v(158.75, 53.97) * mm, "radius": 1.59 * mm});
            skCircle(sketch, "E224.MirrorC", {"center": v(88.9, 60.32) * mm, "radius": 1.59 * mm});
            skCircle(sketch, "E225.MirrorC", {"center": v(95.25, 66.67) * mm, "radius": 1.59 * mm});
            skCircle(sketch, "E226.MirrorC", {"center": v(95.25, 53.97) * mm, "radius": 1.59 * mm});
            skCircle(sketch, "E227.MirrorC", {"center": v(158.75, 60.32) * mm, "radius": 1.59 * mm});
            skCircle(sketch, "E228.MirrorC", {"center": v(250.83, 53.97) * mm, "radius": 1.59 * mm});
            skCircle(sketch, "E229.MirrorC", {"center": v(165.1, 60.32) * mm, "radius": 1.59 * mm});
            skCircle(sketch, "E230.MirrorC", {"center": v(139.7, 53.97) * mm, "radius": 1.59 * mm});
            skCircle(sketch, "E231.MirrorC", {"center": v(285.75, 53.98) * mm, "radius": 1.59 * mm});
            skCircle(sketch, "E232.MirrorC", {"center": v(111.12, 53.97) * mm, "radius": 1.59 * mm});
            skCircle(sketch, "E233.MirrorC", {"center": v(111.12, 66.67) * mm, "radius": 1.59 * mm});
            skCircle(sketch, "E234.MirrorC", {"center": v(193.68, 53.97) * mm, "radius": 1.59 * mm});
            skCircle(sketch, "E235.MirrorC", {"center": v(200.03, 53.97) * mm, "radius": 1.59 * mm});
            skCircle(sketch, "E236.MirrorC", {"center": v(292.1, 73.02) * mm, "radius": 1.59 * mm});
            skCircle(sketch, "E237.MirrorC", {"center": v(304.8, 73.02) * mm, "radius": 1.59 * mm});
            skCircle(sketch, "E238.MirrorC", {"center": v(279.4, 60.32) * mm, "radius": 1.59 * mm});
            skCircle(sketch, "E239.MirrorC", {"center": v(82.55, 53.97) * mm, "radius": 1.59 * mm});
            skCircle(sketch, "E240.MirrorC", {"center": v(152.4, 73.02) * mm, "radius": 1.59 * mm});
            skCircle(sketch, "E241.MirrorC", {"center": v(69.85, 53.97) * mm, "radius": 1.59 * mm});
            skCircle(sketch, "E242.MirrorC", {"center": v(158.75, 73.02) * mm, "radius": 1.59 * mm});
            skCircle(sketch, "E243.MirrorC", {"center": v(209.55, 60.32) * mm, "radius": 1.59 * mm});
            skCircle(sketch, "E244.MirrorC", {"center": v(187.33, 66.67) * mm, "radius": 1.59 * mm});
            skCircle(sketch, "E245.MirrorC", {"center": v(279.4, 53.98) * mm, "radius": 1.59 * mm});
            skCircle(sketch, "E246.MirrorC", {"center": v(257.18, 53.97) * mm, "radius": 1.59 * mm});
            skCircle(sketch, "E247.MirrorC", {"center": v(104.78, 60.32) * mm, "radius": 1.59 * mm});
            skCircle(sketch, "E248.MirrorC", {"center": v(187.33, 73.02) * mm, "radius": 1.59 * mm});
            skCircle(sketch, "E249.MirrorC", {"center": v(215.9, 60.32) * mm, "radius": 1.59 * mm});
            skCircle(sketch, "E250.MirrorC", {"center": v(292.1, 66.67) * mm, "radius": 1.59 * mm});
            skCircle(sketch, "E251.MirrorC", {"center": v(244.48, 60.32) * mm, "radius": 1.59 * mm});
            skCircle(sketch, "E252.MirrorC", {"center": v(123.82, 66.67) * mm, "radius": 1.59 * mm});
            skCircle(sketch, "E253.MirrorC", {"center": v(123.82, 60.32) * mm, "radius": 1.59 * mm});
            skCircle(sketch, "E254.MirrorC", {"center": v(263.53, 73.02) * mm, "radius": 1.59 * mm});
            skCircle(sketch, "E255.MirrorC", {"center": v(146.05, 53.97) * mm, "radius": 1.59 * mm});
            skCircle(sketch, "E256.MirrorC", {"center": v(263.53, 60.32) * mm, "radius": 1.59 * mm});
            skCircle(sketch, "E257.MirrorC", {"center": v(193.68, 73.02) * mm, "radius": 1.59 * mm});
            skCircle(sketch, "E258.MirrorC", {"center": v(298.45, 73.02) * mm, "radius": 1.59 * mm});
            skCircle(sketch, "E259.MirrorC", {"center": v(152.4, 53.97) * mm, "radius": 1.59 * mm});
            skCircle(sketch, "E260.MirrorC", {"center": v(95.25, 73.02) * mm, "radius": 1.59 * mm});
            skCircle(sketch, "E261.MirrorC", {"center": v(292.1, 60.32) * mm, "radius": 1.59 * mm});
            skCircle(sketch, "E262.MirrorC", {"center": v(158.75, 66.67) * mm, "radius": 1.59 * mm});
            skCircle(sketch, "E263.MirrorC", {"center": v(165.1, 66.67) * mm, "radius": 1.59 * mm});
            skCircle(sketch, "E264.MirrorC", {"center": v(193.68, 66.67) * mm, "radius": 1.59 * mm});
            skCircle(sketch, "E265.MirrorC", {"center": v(130.17, 73.02) * mm, "radius": 1.59 * mm});
            skCircle(sketch, "E266.MirrorC", {"center": v(298.45, 60.33) * mm, "radius": 1.59 * mm});
            skCircle(sketch, "E267.MirrorC", {"center": v(76.2, 66.67) * mm, "radius": 1.59 * mm});
            skCircle(sketch, "E268.MirrorC", {"center": v(165.1, 53.97) * mm, "radius": 1.59 * mm});
            skCircle(sketch, "E269.MirrorC", {"center": v(244.48, 53.97) * mm, "radius": 1.59 * mm});
            skCircle(sketch, "E270.MirrorC", {"center": v(298.45, 53.98) * mm, "radius": 1.59 * mm});
            skCircle(sketch, "E271.MirrorC", {"center": v(76.2, 53.97) * mm, "radius": 1.59 * mm});
            skCircle(sketch, "E272.MirrorC", {"center": v(130.17, 66.67) * mm, "radius": 1.59 * mm});
            skCircle(sketch, "E273.MirrorC", {"center": v(200.03, 60.32) * mm, "radius": 1.59 * mm});
            skCircle(sketch, "E274.MirrorC", {"center": v(228.6, 53.97) * mm, "radius": 1.59 * mm});
            skCircle(sketch, "E275.MirrorC", {"center": v(234.95, 66.67) * mm, "radius": 1.59 * mm});
            skCircle(sketch, "E276.MirrorC", {"center": v(234.95, 60.32) * mm, "radius": 1.59 * mm});
            skCircle(sketch, "E277.MirrorC", {"center": v(180.98, 53.97) * mm, "radius": 1.59 * mm});
            skCircle(sketch, "E278.MirrorC", {"center": v(200.03, 66.67) * mm, "radius": 1.59 * mm});
            skCircle(sketch, "E279.MirrorC", {"center": v(222.25, 53.97) * mm, "radius": 1.59 * mm});
            skCircle(sketch, "E280.MirrorC", {"center": v(104.78, 53.97) * mm, "radius": 1.59 * mm});
            skCircle(sketch, "E281.MirrorC", {"center": v(180.98, 66.67) * mm, "radius": 1.59 * mm});
            skCircle(sketch, "E282.MirrorC", {"center": v(111.12, 60.32) * mm, "radius": 1.59 * mm});
            skCircle(sketch, "E283.MirrorC", {"center": v(76.2, 60.32) * mm, "radius": 1.59 * mm});
            skCircle(sketch, "E284.MirrorC", {"center": v(146.05, 60.32) * mm, "radius": 1.59 * mm});
            skCircle(sketch, "E285.MirrorC", {"center": v(250.83, 66.67) * mm, "radius": 1.59 * mm});
            skCircle(sketch, "E286.MirrorC", {"center": v(234.95, 73.02) * mm, "radius": 1.59 * mm});
            skCircle(sketch, "E287.MirrorC", {"center": v(152.4, 66.67) * mm, "radius": 1.59 * mm});
            skCircle(sketch, "E288.MirrorC", {"center": v(215.9, 53.97) * mm, "radius": 1.59 * mm});
            skCircle(sketch, "E289.MirrorC", {"center": v(269.88, 53.97) * mm, "radius": 1.59 * mm});
            skCircle(sketch, "E290.MirrorC", {"center": v(117.47, 53.97) * mm, "radius": 1.59 * mm});
            skCircle(sketch, "E291.MirrorC", {"center": v(269.88, 66.67) * mm, "radius": 1.59 * mm});
            skCircle(sketch, "E292.MirrorC", {"center": v(222.25, 73.02) * mm, "radius": 1.59 * mm});
            skCircle(sketch, "E293.MirrorC", {"center": v(222.25, 66.67) * mm, "radius": 1.59 * mm});
            skCircle(sketch, "E294.MirrorC", {"center": v(117.47, 60.32) * mm, "radius": 1.59 * mm});
            skCircle(sketch, "E295.MirrorC", {"center": v(174.63, 60.32) * mm, "radius": 1.59 * mm});
            skCircle(sketch, "E296.MirrorC", {"center": v(95.25, 60.32) * mm, "radius": 1.59 * mm});
            skCircle(sketch, "E297.MirrorC", {"center": v(200.03, 73.02) * mm, "radius": 1.59 * mm});
            skCircle(sketch, "E298.MirrorC", {"center": v(130.17, 53.97) * mm, "radius": 1.59 * mm});
            skCircle(sketch, "E299.MirrorC", {"center": v(193.68, 60.32) * mm, "radius": 1.59 * mm});
            skCircle(sketch, "E300.MirrorC", {"center": v(285.75, 60.32) * mm, "radius": 1.59 * mm});
            skCircle(sketch, "E301.MirrorC", {"center": v(304.8, 66.67) * mm, "radius": 1.59 * mm});
            skCircle(sketch, "E302.MirrorC", {"center": v(285.75, 66.67) * mm, "radius": 1.59 * mm});
            skCircle(sketch, "E303.MirrorC", {"center": v(257.18, 73.02) * mm, "radius": 1.59 * mm});
            skCircle(sketch, "E304.MirrorC", {"center": v(269.88, 73.02) * mm, "radius": 1.59 * mm});
            skCircle(sketch, "E305.MirrorC", {"center": v(304.8, 53.98) * mm, "radius": 1.59 * mm});
            skCircle(sketch, "E306.MirrorC", {"center": v(82.55, 66.67) * mm, "radius": 1.59 * mm});
            skCircle(sketch, "E307.MirrorC", {"center": v(209.55, 53.97) * mm, "radius": 1.59 * mm});
            skCircle(sketch, "E308.MirrorC", {"center": v(298.45, 66.67) * mm, "radius": 1.59 * mm});
            skCircle(sketch, "E309.MirrorC", {"center": v(130.17, 60.32) * mm, "radius": 1.59 * mm});
            skCircle(sketch, "E310.MirrorC", {"center": v(234.95, 53.97) * mm, "radius": 1.59 * mm});
            skCircle(sketch, "E311.MirrorC", {"center": v(88.9, 66.67) * mm, "radius": 1.59 * mm});
            skCircle(sketch, "E312.MirrorC", {"center": v(222.25, 60.32) * mm, "radius": 1.59 * mm});
            skCircle(sketch, "E313.MirrorC", {"center": v(139.7, 60.32) * mm, "radius": 1.59 * mm});
            skCircle(sketch, "E314.MirrorC", {"center": v(174.63, 53.97) * mm, "radius": 1.59 * mm});
            skCircle(sketch, "E315.MirrorC", {"center": v(228.6, 66.67) * mm, "radius": 1.59 * mm});
            skCircle(sketch, "E316.MirrorC", {"center": v(69.85, 60.32) * mm, "radius": 1.59 * mm});
            skCircle(sketch, "E317.MirrorC", {"center": v(250.83, 60.32) * mm, "radius": 1.59 * mm});
            skLineSegment(sketch, "E318.MirrorCS", {"start": v(88.9, 53.97) * mm, "end": v(123.82, 53.97) * mm, "construction": true});
            skLineSegment(sketch, "E319", {"start": v(314.32, 63.5) * mm, "end": v(322.39, 63.5) * mm});
            skCircle(sketch, "E320.1.0.0", {"center": v(314.33, 101.6) * mm, "radius": 1.59 * mm});
            skCircle(sketch, "E320.1.0.1", {"center": v(314.33, 107.95) * mm, "radius": 1.59 * mm});
            skCircle(sketch, "E320.1.0.2", {"center": v(314.33, 114.3) * mm, "radius": 1.59 * mm});
            skCircle(sketch, "E320.1.0.3", {"center": v(314.33, 95.25) * mm, "radius": 1.59 * mm});
            skLineSegment(sketch, "E320.direction1", {"start": v(304.8, 101.6) * mm, "end": v(314.33, 101.6) * mm, "construction": true});
            skCircle(sketch, "E321.1.0", {"center": v(331.7, 111.24) * mm, "radius": 1.59 * mm});
            skCircle(sketch, "E321.1.1", {"center": v(325.18, 93.34) * mm, "radius": 1.59 * mm});
            skLineSegment(sketch, "E321.1.2", {"start": v(318.4, 102.56) * mm, "end": v(327.36, 99.3) * mm, "construction": true});
            skCircle(sketch, "E321.1.3", {"center": v(329.53, 105.27) * mm, "radius": 1.59 * mm});
            skCircle(sketch, "E321.1.4", {"center": v(327.36, 99.3) * mm, "radius": 1.59 * mm});
            skCircle(sketch, "E321.2.0", {"center": v(346.98, 102.42) * mm, "radius": 1.59 * mm});
            skCircle(sketch, "E321.2.1", {"center": v(334.73, 87.82) * mm, "radius": 1.59 * mm});
            skLineSegment(sketch, "E321.2.2", {"start": v(331.52, 98.8) * mm, "end": v(338.82, 92.69) * mm, "construction": true});
            skCircle(sketch, "E321.2.3", {"center": v(342.9, 97.55) * mm, "radius": 1.59 * mm});
            skCircle(sketch, "E321.2.4", {"center": v(338.82, 92.69) * mm, "radius": 1.59 * mm});
            skCircle(sketch, "E321.3.0", {"center": v(358.32, 88.9) * mm, "radius": 1.59 * mm});
            skCircle(sketch, "E321.3.1", {"center": v(341.82, 79.38) * mm, "radius": 1.59 * mm});
            skLineSegment(sketch, "E321.3.2", {"start": v(342.56, 90.8) * mm, "end": v(347.32, 82.55) * mm, "construction": true});
            skCircle(sketch, "E321.3.3", {"center": v(352.82, 85.72) * mm, "radius": 1.59 * mm});
            skCircle(sketch, "E321.3.4", {"center": v(347.32, 82.55) * mm, "radius": 1.59 * mm});
            skCircle(sketch, "E321.4.0", {"center": v(364.35, 72.32) * mm, "radius": 1.59 * mm});
            skCircle(sketch, "E321.4.1", {"center": v(345.6, 69.01) * mm, "radius": 1.59 * mm});
            skLineSegment(sketch, "E321.4.2", {"start": v(350.2, 79.5) * mm, "end": v(351.85, 70.12) * mm, "construction": true});
            skCircle(sketch, "E321.4.3", {"center": v(358.1, 71.22) * mm, "radius": 1.59 * mm});
            skCircle(sketch, "E321.4.4", {"center": v(351.85, 70.12) * mm, "radius": 1.59 * mm});
            skCircle(sketch, "E321.5.0", {"center": v(364.35, 54.68) * mm, "radius": 1.59 * mm});
            skCircle(sketch, "E321.5.1", {"center": v(345.6, 57.99) * mm, "radius": 1.59 * mm});
            skLineSegment(sketch, "E321.5.2", {"start": v(353.5, 66.26) * mm, "end": v(351.85, 56.88) * mm, "construction": true});
            skCircle(sketch, "E321.5.3", {"center": v(358.1, 55.78) * mm, "radius": 1.59 * mm});
            skCircle(sketch, "E321.5.4", {"center": v(351.85, 56.88) * mm, "radius": 1.59 * mm});
            skCircle(sketch, "E321.6.0", {"center": v(358.32, 38.1) * mm, "radius": 1.59 * mm});
            skCircle(sketch, "E321.6.1", {"center": v(341.82, 47.62) * mm, "radius": 1.59 * mm});
            skLineSegment(sketch, "E321.6.2", {"start": v(352.08, 52.7) * mm, "end": v(347.32, 44.45) * mm, "construction": true});
            skCircle(sketch, "E321.6.3", {"center": v(352.82, 41.27) * mm, "radius": 1.59 * mm});
            skCircle(sketch, "E321.6.4", {"center": v(347.32, 44.45) * mm, "radius": 1.59 * mm});
            skCircle(sketch, "E321.7.0", {"center": v(346.98, 24.58) * mm, "radius": 1.59 * mm});
            skCircle(sketch, "E321.7.1", {"center": v(334.73, 39.18) * mm, "radius": 1.59 * mm});
            skLineSegment(sketch, "E321.7.2", {"start": v(346.11, 40.44) * mm, "end": v(338.82, 34.31) * mm, "construction": true});
            skCircle(sketch, "E321.7.3", {"center": v(342.9, 29.45) * mm, "radius": 1.59 * mm});
            skCircle(sketch, "E321.7.4", {"center": v(338.82, 34.31) * mm, "radius": 1.59 * mm});
            skCircle(sketch, "E321.8.0", {"center": v(331.7, 15.76) * mm, "radius": 1.59 * mm});
            skCircle(sketch, "E321.8.1", {"center": v(325.18, 33.66) * mm, "radius": 1.59 * mm});
            skLineSegment(sketch, "E321.8.2", {"start": v(336.3, 30.96) * mm, "end": v(327.36, 27.7) * mm, "construction": true});
            skCircle(sketch, "E321.8.3", {"center": v(329.53, 21.73) * mm, "radius": 1.59 * mm});
            skCircle(sketch, "E321.8.4", {"center": v(327.36, 27.7) * mm, "radius": 1.59 * mm});
            skCircle(sketch, "E321.9.0", {"center": v(314.32, 12.7) * mm, "radius": 1.59 * mm});
            skCircle(sketch, "E321.9.1", {"center": v(314.32, 31.75) * mm, "radius": 1.59 * mm});
            skLineSegment(sketch, "E321.9.2", {"start": v(323.85, 25.4) * mm, "end": v(314.32, 25.4) * mm, "construction": true});
            skCircle(sketch, "E321.9.3", {"center": v(314.32, 19.05) * mm, "radius": 1.59 * mm});
            skCircle(sketch, "E321.9.4", {"center": v(314.32, 25.4) * mm, "radius": 1.59 * mm});
            skPoint(sketch, "E321.center", {"position": v(314.32, 63.5) * mm});
            skLineSegment(sketch, "E321.anchor1", {"start": v(314.32, 63.5) * mm, "end": v(314.33, 114.3) * mm, "construction": true});
            skLineSegment(sketch, "E321.anchor2", {"start": v(314.32, 63.5) * mm, "end": v(314.32, 12.7) * mm, "construction": true});
            skLineSegment(sketch, "E322", {"start": v(69.85, 53.97) * mm, "end": v(69.85, 31.75) * mm});
            skLineSegment(sketch, "E323", {"start": v(69.85, 42.86) * mm, "end": v(60.32, 42.86) * mm});
            skCircle(sketch, "E324.1.0.0", {"center": v(60.32, 73.02) * mm, "radius": 1.59 * mm});
            skCircle(sketch, "E324.1.0.1", {"center": v(60.32, 53.97) * mm, "radius": 1.59 * mm});
            skCircle(sketch, "E324.1.0.2", {"center": v(60.32, 66.67) * mm, "radius": 1.59 * mm});
            skCircle(sketch, "E324.1.0.3", {"center": v(60.32, 60.32) * mm, "radius": 1.59 * mm});
            skLineSegment(sketch, "E324.1.0.4", {"start": v(60.32, 73.02) * mm, "end": v(60.32, 66.67) * mm, "construction": true});
            skLineSegment(sketch, "E324.direction1", {"start": v(69.85, 73.02) * mm, "end": v(60.32, 73.02) * mm, "construction": true});
            skCircle(sketch, "E325.1.0", {"center": v(47.98, 55.21) * mm, "radius": 1.59 * mm});
            skCircle(sketch, "E325.1.1", {"center": v(39, 64.2) * mm, "radius": 1.59 * mm});
            skLineSegment(sketch, "E325.1.2", {"start": v(39, 64.2) * mm, "end": v(43.49, 59.7) * mm, "construction": true});
            skCircle(sketch, "E325.1.3", {"center": v(43.49, 59.7) * mm, "radius": 1.59 * mm});
            skCircle(sketch, "E325.1.4", {"center": v(52.47, 50.72) * mm, "radius": 1.59 * mm});
            skCircle(sketch, "E325.2.0", {"center": v(42.86, 42.86) * mm, "radius": 1.59 * mm});
            skCircle(sketch, "E325.2.1", {"center": v(30.16, 42.86) * mm, "radius": 1.59 * mm});
            skLineSegment(sketch, "E325.2.2", {"start": v(30.16, 42.86) * mm, "end": v(36.51, 42.86) * mm, "construction": true});
            skCircle(sketch, "E325.2.3", {"center": v(36.51, 42.86) * mm, "radius": 1.59 * mm});
            skCircle(sketch, "E325.2.4", {"center": v(49.21, 42.86) * mm, "radius": 1.59 * mm});
            skCircle(sketch, "E325.3.0", {"center": v(47.98, 30.51) * mm, "radius": 1.59 * mm});
            skCircle(sketch, "E325.3.1", {"center": v(39, 21.53) * mm, "radius": 1.59 * mm});
            skLineSegment(sketch, "E325.3.2", {"start": v(39, 21.53) * mm, "end": v(43.49, 26.02) * mm, "construction": true});
            skCircle(sketch, "E325.3.3", {"center": v(43.49, 26.02) * mm, "radius": 1.59 * mm});
            skCircle(sketch, "E325.3.4", {"center": v(52.47, 35) * mm, "radius": 1.59 * mm});
            skCircle(sketch, "E325.4.0", {"center": v(60.33, 25.4) * mm, "radius": 1.59 * mm});
            skCircle(sketch, "E325.4.1", {"center": v(60.33, 12.7) * mm, "radius": 1.59 * mm});
            skLineSegment(sketch, "E325.4.2", {"start": v(60.33, 12.7) * mm, "end": v(60.33, 19.05) * mm, "construction": true});
            skCircle(sketch, "E325.4.3", {"center": v(60.33, 19.05) * mm, "radius": 1.59 * mm});
            skCircle(sketch, "E325.4.4", {"center": v(60.33, 31.75) * mm, "radius": 1.59 * mm});
            skPoint(sketch, "E325.center", {"position": v(60.32, 42.86) * mm});
            skLineSegment(sketch, "E325.anchor1", {"start": v(60.32, 42.86) * mm, "end": v(60.32, 60.32) * mm, "construction": true});
            skLineSegment(sketch, "E325.anchor2", {"start": v(60.33, 42.86) * mm, "end": v(60.33, 25.4) * mm, "construction": true});
            skCircle(sketch, "E326", {"center": v(322.39, 63.5) * mm, "radius": 1.59 * mm});
            skCircle(sketch, "E327", {"center": v(-12.7, 114.3) * mm, "radius": 1.59 * mm});
            skCircle(sketch, "E328.0.1.0", {"center": v(-12.7, 103.01) * mm, "radius": 1.59 * mm});
            skCircle(sketch, "E328.0.2.0", {"center": v(-12.7, 91.72) * mm, "radius": 1.59 * mm});
            skCircle(sketch, "E328.0.3.0", {"center": v(-12.7, 80.43) * mm, "radius": 1.59 * mm});
            skCircle(sketch, "E328.0.4.0", {"center": v(-12.7, 69.14) * mm, "radius": 1.59 * mm});
            skCircle(sketch, "E328.0.5.0", {"center": v(-12.7, 57.86) * mm, "radius": 1.59 * mm});
            skCircle(sketch, "E328.0.6.0", {"center": v(-12.7, 46.57) * mm, "radius": 1.59 * mm});
            skCircle(sketch, "E328.0.7.0", {"center": v(-12.7, 35.28) * mm, "radius": 1.59 * mm});
            skCircle(sketch, "E328.0.8.0", {"center": v(-12.7, 23.99) * mm, "radius": 1.59 * mm});
            skCircle(sketch, "E328.0.9.0", {"center": v(-12.7, 12.7) * mm, "radius": 1.59 * mm});
            skCircle(sketch, "E328.1.0.0", {"center": v(-6.35, 114.3) * mm, "radius": 1.59 * mm});
            skCircle(sketch, "E328.1.1.0", {"center": v(-6.35, 103.01) * mm, "radius": 1.59 * mm});
            skCircle(sketch, "E328.1.2.0", {"center": v(-6.35, 91.72) * mm, "radius": 1.59 * mm});
            skCircle(sketch, "E328.1.3.0", {"center": v(-6.35, 80.43) * mm, "radius": 1.59 * mm});
            skCircle(sketch, "E328.1.4.0", {"center": v(-6.35, 69.14) * mm, "radius": 1.59 * mm});
            skCircle(sketch, "E328.1.5.0", {"center": v(-6.35, 57.86) * mm, "radius": 1.59 * mm});
            skCircle(sketch, "E328.1.6.0", {"center": v(-6.35, 46.57) * mm, "radius": 1.59 * mm});
            skCircle(sketch, "E328.1.7.0", {"center": v(-6.35, 35.28) * mm, "radius": 1.59 * mm});
            skCircle(sketch, "E328.1.8.0", {"center": v(-6.35, 23.99) * mm, "radius": 1.59 * mm});
            skCircle(sketch, "E328.1.9.0", {"center": v(-6.35, 12.7) * mm, "radius": 1.59 * mm});
            skCircle(sketch, "E328.2.0.0", {"center": v(0, 114.3) * mm, "radius": 1.59 * mm});
            skCircle(sketch, "E328.2.1.0", {"center": v(0, 103.01) * mm, "radius": 1.59 * mm});
            skCircle(sketch, "E328.2.2.0", {"center": v(0, 91.72) * mm, "radius": 1.59 * mm});
            skCircle(sketch, "E328.2.3.0", {"center": v(0, 80.43) * mm, "radius": 1.59 * mm});
            skCircle(sketch, "E328.2.4.0", {"center": v(0, 69.14) * mm, "radius": 1.59 * mm});
            skCircle(sketch, "E328.2.5.0", {"center": v(0, 57.86) * mm, "radius": 1.59 * mm});
            skCircle(sketch, "E328.2.6.0", {"center": v(0, 46.57) * mm, "radius": 1.59 * mm});
            skCircle(sketch, "E328.2.7.0", {"center": v(0, 35.28) * mm, "radius": 1.59 * mm});
            skCircle(sketch, "E328.2.8.0", {"center": v(0, 23.99) * mm, "radius": 1.59 * mm});
            skCircle(sketch, "E328.2.9.0", {"center": v(0, 12.7) * mm, "radius": 1.59 * mm});
            skCircle(sketch, "E328.3.0.0", {"center": v(6.35, 114.3) * mm, "radius": 1.59 * mm});
            skCircle(sketch, "E328.3.1.0", {"center": v(6.35, 103.01) * mm, "radius": 1.59 * mm});
            skCircle(sketch, "E328.3.2.0", {"center": v(6.35, 91.72) * mm, "radius": 1.59 * mm});
            skCircle(sketch, "E328.3.3.0", {"center": v(6.35, 80.43) * mm, "radius": 1.59 * mm});
            skCircle(sketch, "E328.3.4.0", {"center": v(6.35, 69.14) * mm, "radius": 1.59 * mm});
            skCircle(sketch, "E328.3.5.0", {"center": v(6.35, 57.86) * mm, "radius": 1.59 * mm});
            skCircle(sketch, "E328.3.6.0", {"center": v(6.35, 46.57) * mm, "radius": 1.59 * mm});
            skCircle(sketch, "E328.3.7.0", {"center": v(6.35, 35.28) * mm, "radius": 1.59 * mm});
            skCircle(sketch, "E328.3.8.0", {"center": v(6.35, 23.99) * mm, "radius": 1.59 * mm});
            skCircle(sketch, "E328.3.9.0", {"center": v(6.35, 12.7) * mm, "radius": 1.59 * mm});
            skLineSegment(sketch, "E328.direction1", {"start": v(-12.7, 114.3) * mm, "end": v(-6.35, 114.3) * mm, "construction": true});
            skLineSegment(sketch, "E328.direction2", {"start": v(-12.7, 114.3) * mm, "end": v(-12.7, 103.01) * mm, "construction": true});
            skCircle(sketch, "E329", {"center": v(28.57, 114.3) * mm, "radius": 1.59 * mm});
            skCircle(sketch, "E330.0.1.0", {"center": v(28.57, 107.95) * mm, "radius": 1.59 * mm});
            skCircle(sketch, "E330.0.2.0", {"center": v(28.57, 101.6) * mm, "radius": 1.59 * mm});
            skCircle(sketch, "E330.0.3.0", {"center": v(28.57, 95.25) * mm, "radius": 1.59 * mm});
            skCircle(sketch, "E330.1.0.0", {"center": v(38.1, 114.3) * mm, "radius": 1.59 * mm});
            skCircle(sketch, "E330.1.1.0", {"center": v(38.1, 107.95) * mm, "radius": 1.59 * mm});
            skCircle(sketch, "E330.1.2.0", {"center": v(38.1, 101.6) * mm, "radius": 1.59 * mm});
            skCircle(sketch, "E330.1.3.0", {"center": v(38.1, 95.25) * mm, "radius": 1.59 * mm});
            skCircle(sketch, "E330.2.0.0", {"center": v(47.62, 114.3) * mm, "radius": 1.59 * mm});
            skCircle(sketch, "E330.2.1.0", {"center": v(47.62, 107.95) * mm, "radius": 1.59 * mm});
            skCircle(sketch, "E330.2.2.0", {"center": v(47.62, 101.6) * mm, "radius": 1.59 * mm});
            skCircle(sketch, "E330.2.3.0", {"center": v(47.62, 95.25) * mm, "radius": 1.59 * mm});
            skLineSegment(sketch, "E330.direction1", {"start": v(22.22, 114.3) * mm, "end": v(31.75, 114.3) * mm, "construction": true});
            skLineSegment(sketch, "E330.direction2", {"start": v(22.22, 114.3) * mm, "end": v(22.22, 107.95) * mm, "construction": true});
            skSolve(sketch);
        }
        {
            var Q0;
            Q0 = qSketchRegion(id + "F2", true);
            extrude(context, id + "F3", {"entities" : qUnion([Q0]), "operationType" : NewBodyOperationType.REMOVE, "oppositeDirection" : true, "depth" : 9.52 * mm});
        }
    });
